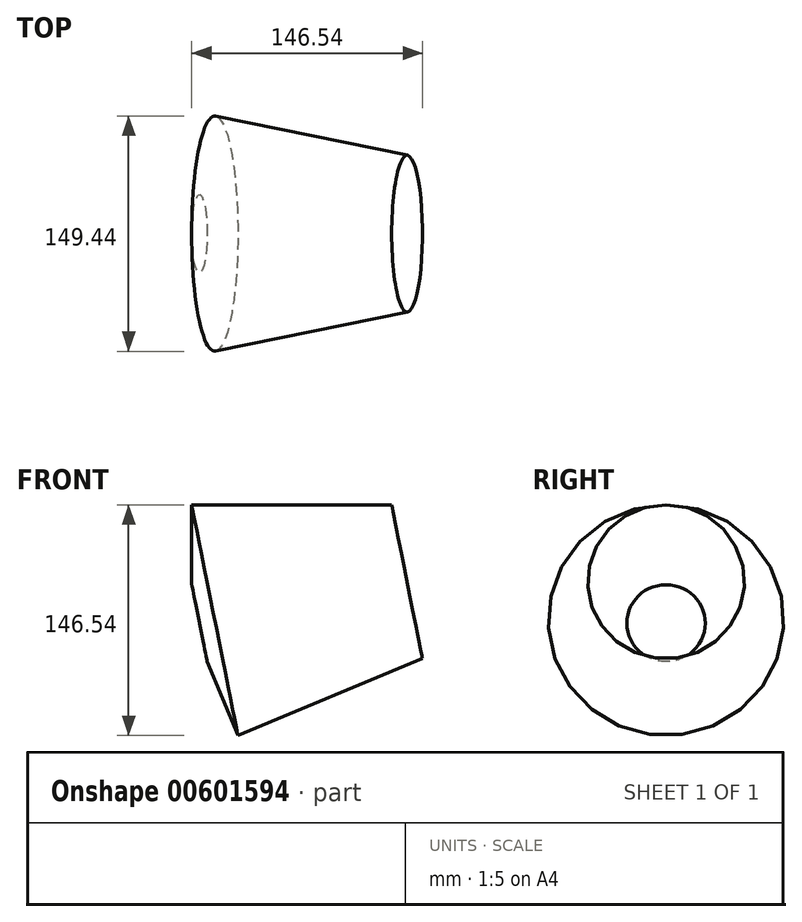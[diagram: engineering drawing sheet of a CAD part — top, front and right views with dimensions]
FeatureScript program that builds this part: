
annotation { "Feature Type Name" : "Feature", "Feature Type Description" : "" }
export const myFeature = defineFeature(function(context is Context, id is Id, definition is map)
    precondition{}
    {
        {
            var Q0;
            Q0=qCreatedBy(makeId("Front.planeOp"),FACE);
            var sketch = newSketch(context, id + "F0", { "sketchPlane" : qUnion([Q0])});
            skLineSegment(sketch, "E0.bottom", {"start": v(-63.5, 25.4) * mm, "end": v(63.5, 25.4) * mm});
            skLineSegment(sketch, "E0.top", {"start": v(-63.5, -25.4) * mm, "end": v(63.5, -25.4) * mm});
            skLineSegment(sketch, "E0.left", {"start": v(-63.5, 25.4) * mm, "end": v(-63.5, -25.4) * mm});
            skLineSegment(sketch, "E0.right", {"start": v(63.5, 25.4) * mm, "end": v(63.5, -25.4) * mm});
            skLineSegment(sketch, "E1", {"start": v(0, 0) * mm, "end": v(79.16, 0) * mm, "construction": true});
            skLineSegment(sketch, "E2", {"start": v(0, 0) * mm, "end": v(0, 47.87) * mm, "construction": true});
            skLineSegment(sketch, "E3", {"start": v(63.5, -25.4) * mm, "end": v(-63.5, -50.8) * mm, "construction": true});
            skSolve(sketch);
        }
        {
            var Q0;
            Q0=makeQuery(id+"F0.imprint","IMPRINT",FACE,{"disambiguationData":[TD([[makeQuery(id+"F0.imprint","IMPRINT",EDGE,{"derivedFrom":sQuery(id+"F0.wireOp",EDGE,"E0.bottom")}),-1.0]])]});
            var Q1;
            Q1=sQuery(id+"F0.wireOp",EDGE,"E0.left");
            var Q2;
            Q2=sQuery(id+"F0.wireOp",EDGE,"E0.bottom");
            var Q3;
            Q3=sQuery(id+"F0.wireOp",EDGE,"E3");
            revolve(context, id + "F1", {"bodyType" : ToolBodyType.SURFACE, "entities" : qUnion([Q0]), "surfaceEntities" : qUnion([Q1, Q2]), "axis" : qUnion([Q3]), "revolveType" : RevolveType.FULL});
        }
    });
